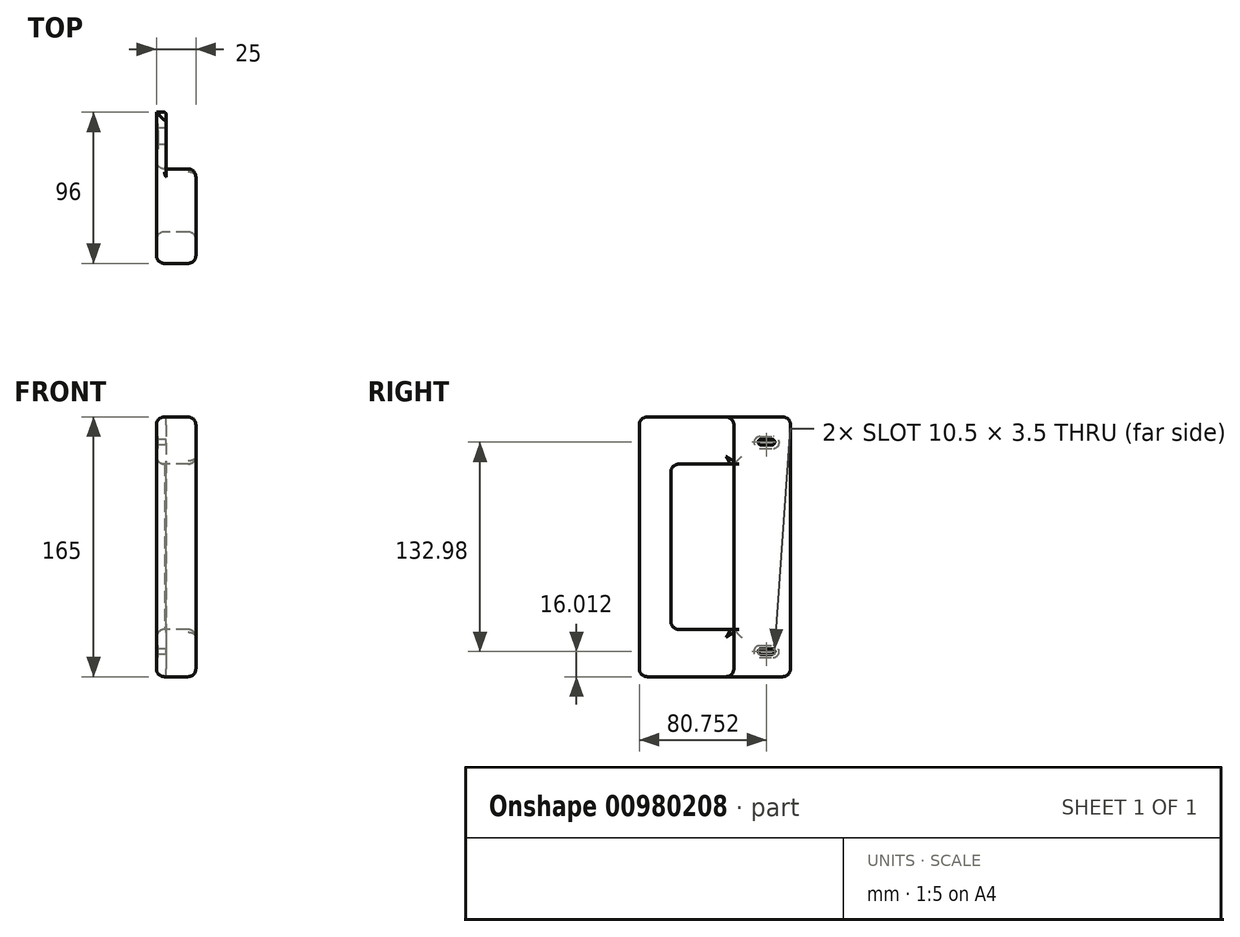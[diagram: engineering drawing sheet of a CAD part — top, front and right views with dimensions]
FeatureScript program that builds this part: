
annotation { "Feature Type Name" : "Feature", "Feature Type Description" : "" }
export const myFeature = defineFeature(function(context is Context, id is Id, definition is map)
    precondition{}
    {
        {
            var Q0;
            Q0=qCreatedBy(makeId("Right.planeOp"),FACE);
            var sketch = newSketch(context, id + "F0", { "sketchPlane" : qUnion([Q0])});
            skLineSegment(sketch, "E0.bottom", {"start": v(74.02, 103.51) * mm, "end": v(38.02, 103.51) * mm});
            skLineSegment(sketch, "E0.top", {"start": v(74.02, -61.49) * mm, "end": v(38.02, -61.49) * mm});
            skLineSegment(sketch, "E0.left", {"start": v(74.02, 103.51) * mm, "end": v(74.02, -61.49) * mm});
            skLineSegment(sketch, "E0.right", {"start": v(38.02, 103.51) * mm, "end": v(38.02, -61.49) * mm});
            skLineSegment(sketch, "E1", {"start": v(74.02, 21.01) * mm, "end": v(38.02, 21.01) * mm, "construction": true});
            skArc(sketch, "E2.0.startCap", {"start": v(62.27, 89.25) * mm, "mid": v(64.02, 87.5) * mm, "end": v(62.27, 85.75) * mm});
            skPoint(sketch, "E3", {"position": v(64.02, 87.5) * mm});
            skPoint(sketch, "E4", {"position": v(53.52, 87.5) * mm});
            skArc(sketch, "E5.0.startCap", {"start": v(55.27, 85.75) * mm, "mid": v(53.52, 87.5) * mm, "end": v(55.27, 89.25) * mm});
            skLineSegment(sketch, "E6", {"start": v(62.27, 89.25) * mm, "end": v(55.27, 89.25) * mm});
            skLineSegment(sketch, "E7", {"start": v(55.27, 85.75) * mm, "end": v(62.27, 85.75) * mm});
            skArc(sketch, "E8.MirrorCS", {"start": v(55.27, -43.73) * mm, "mid": v(53.52, -45.48) * mm, "end": v(55.27, -47.23) * mm});
            skArc(sketch, "E9.MirrorCS", {"start": v(62.27, -47.23) * mm, "mid": v(64.02, -45.48) * mm, "end": v(62.27, -43.73) * mm});
            skPoint(sketch, "E10.MirrorP", {"position": v(64.02, -45.48) * mm});
            skLineSegment(sketch, "E11.MirrorCS", {"start": v(62.27, -47.23) * mm, "end": v(55.27, -47.23) * mm});
            skLineSegment(sketch, "E12.MirrorCS", {"start": v(55.27, -43.73) * mm, "end": v(62.27, -43.73) * mm});
            skLineSegment(sketch, "E13.MirrorCS", {"start": v(74.02, -61.49) * mm, "end": v(74.02, 103.51) * mm});
            skSolve(sketch);
        }
        {
            var Q0;
            Q0=qCreatedBy(makeId("Right.planeOp"),FACE);
            var sketch = newSketch(context, id + "F1", { "sketchPlane" : qUnion([Q0])});
            skLineSegment(sketch, "E14.bottom", {"start": v(38.02, 103.51) * mm, "end": v(-21.98, 103.51) * mm});
            skLineSegment(sketch, "E14.top", {"start": v(38.02, -61.49) * mm, "end": v(-21.98, -61.49) * mm});
            skLineSegment(sketch, "E14.left", {"start": v(38.02, 103.51) * mm, "end": v(38.02, -61.49) * mm});
            skLineSegment(sketch, "E14.right", {"start": v(-21.98, 103.51) * mm, "end": v(-21.98, -61.49) * mm});
            skLineSegment(sketch, "E15.bottom", {"start": v(38.02, 73.51) * mm, "end": v(-1.98, 73.51) * mm});
            skLineSegment(sketch, "E15.top", {"start": v(38.02, -31.49) * mm, "end": v(-1.98, -31.49) * mm});
            skLineSegment(sketch, "E15.left", {"start": v(38.02, 73.51) * mm, "end": v(38.02, -31.49) * mm});
            skLineSegment(sketch, "E15.right", {"start": v(-1.98, 73.51) * mm, "end": v(-1.98, -31.49) * mm});
            skLineSegment(sketch, "E16", {"start": v(-21.98, 21.01) * mm, "end": v(38.02, 21.01) * mm, "construction": true});
            skSolve(sketch);
        }
        {
            var Q0;
            {var subQ4=sQuery(id+"F1.wireOp",EDGE,"E14.bottom");Q0=makeQuery(id+"F1.imprint","IMPRINT",FACE,{"disambiguationData":[TD([[makeQuery(id+"F1.imprint","IMPRINT",EDGE,{"derivedFrom":subQ4}),1.0]])]});}
            extrude(context, id + "F2", {"entities" : qUnion([Q0]), "depth" : 25 * mm, "offsetDistance" : 25 * mm});
        }
        {
            var Q0;
            Q0=makeQuery(id+"F0.imprint","IMPRINT",FACE,{"disambiguationData":[TD([[makeQuery(id+"F0.imprint","IMPRINT",EDGE,{"derivedFrom":sQuery(id+"F0.wireOp",EDGE,"E0.bottom")}),1.0]])]});
            extrude(context, id + "F3", {"entities" : qUnion([Q0]), "operationType" : NewBodyOperationType.ADD, "depth" : 6 * mm, "offsetDistance" : 25 * mm});
        }
        {
            var Q0;
            Q0=qCreatedBy(makeId("Right.planeOp"),FACE);
            var sketch = newSketch(context, id + "F4", { "sketchPlane" : qUnion([Q0])});
            skLineSegment(sketch, "E17", {"start": v(54.6, 91.01) * mm, "end": v(63.15, 91.01) * mm});
            skLineSegment(sketch, "E18", {"start": v(54.6, 83.51) * mm, "end": v(63.15, 83.51) * mm});
            skArc(sketch, "E19", {"start": v(63.15, 91.01) * mm, "mid": v(66.9, 87.26) * mm, "end": v(63.15, 83.51) * mm});
            skArc(sketch, "E20", {"start": v(54.6, 91.01) * mm, "mid": v(50.84, 87.26) * mm, "end": v(54.6, 83.51) * mm});
            skLineSegment(sketch, "E21", {"start": v(54.42, -41.78) * mm, "end": v(62.97, -41.78) * mm});
            skLineSegment(sketch, "E22", {"start": v(54.42, -49.28) * mm, "end": v(62.97, -49.28) * mm});
            skArc(sketch, "E23", {"start": v(62.97, -41.78) * mm, "mid": v(66.72, -45.53) * mm, "end": v(62.97, -49.28) * mm});
            skArc(sketch, "E24", {"start": v(54.42, -41.78) * mm, "mid": v(50.67, -45.53) * mm, "end": v(54.42, -49.28) * mm});
            skSolve(sketch);
        }
        {
            var Q0;
            Q0 = qSketchRegion(id + "F4", true);
            extrude(context, id + "F5", {"entities" : qUnion([Q0]), "operationType" : NewBodyOperationType.REMOVE, "oppositeDirection" : true, "depth" : -1 * mm, "offsetDistance" : 25 * mm});
        }
        {
            var Q0;
            Q0=makeQuery(id+"F2.opExtrude","CAP_EDGE",EDGE,{"disambiguationData":[OSD([sQuery(id+"F1.wireOp",EDGE,"E15.right")])],"isStart":true});
            var Q1;
            Q1=makeQuery(id+"F2.opExtrude","CAP_EDGE",EDGE,{"disambiguationData":[OSD([sQuery(id+"F1.wireOp",EDGE,"E15.top")])],"isStart":true});
            var Q2;
            Q2=makeQuery(id+"F3.opExtrude","CAP_EDGE",EDGE,{"disambiguationData":[OSD([sQuery(id+"F0.wireOp",EDGE,"E0.right")])],"isStart":true});
            var Q3;
            Q3=makeQuery(id+"F2.opExtrude","CAP_EDGE",EDGE,{"disambiguationData":[OSD([sQuery(id+"F1.wireOp",EDGE,"E15.bottom")])],"isStart":true});
            var Q4;
            Q4=makeQuery(id+"F2.opExtrude","CAP_EDGE",EDGE,{"disambiguationData":[OSD([sQuery(id+"F1.wireOp",EDGE,"E15.right")])],"isStart":false});
            var Q5;
            Q5=makeQuery(id+"F2.opExtrude","CAP_EDGE",EDGE,{"disambiguationData":[OSD([sQuery(id+"F1.wireOp",EDGE,"E15.top")])],"isStart":false});
            var Q6;
            {var subQ0=sQuery(id+"F1.wireOp",EDGE,"E14.left");Q6=makeQuery(id+"F2.opExtrude","CAP_EDGE",EDGE,{"disambiguationData":[OSD([subQ0]),TDD([makeQuery(id+"F1.imprint","IMPRINT",EDGE,{"disambiguationData":[TD([[makeQuery(id+"F1.imprint","INTERSECT",VERTEX,{"derivedFrom":[sQuery(id+"F1.wireOp",EDGE,"E14.top"),subQ0]}),1.0]])],"derivedFrom":subQ0})])],"isStart":false});}
            var Q7;
            Q7=makeQuery(id+"F2.opExtrude","CAP_EDGE",EDGE,{"disambiguationData":[OSD([sQuery(id+"F1.wireOp",EDGE,"E15.bottom")])],"isStart":false});
            var Q8;
            Q8=makeQuery(id+"F2.opExtrude","SWEPT_EDGE",EDGE,{"disambiguationData":[OSD([sQuery(id+"F1.wireOp",EDGE,"E14.bottom"),sQuery(id+"F1.wireOp",EDGE,"E14.left")])]});
            var Q9;
            {var subQ0=sQuery(id+"F1.wireOp",EDGE,"E14.left");Q9=makeQuery(id+"F2.opExtrude","CAP_EDGE",EDGE,{"disambiguationData":[OSD([subQ0]),TDD([makeQuery(id+"F1.imprint","IMPRINT",EDGE,{"disambiguationData":[TD([[makeQuery(id+"F1.imprint","INTERSECT",VERTEX,{"derivedFrom":[sQuery(id+"F1.wireOp",EDGE,"E14.bottom"),subQ0]}),-1.0]])],"derivedFrom":subQ0})])],"isStart":false});}
            var Q10;
            Q10=makeQuery(id+"F2.opExtrude","CAP_EDGE",EDGE,{"disambiguationData":[OSD([sQuery(id+"F1.wireOp",EDGE,"E14.bottom")])],"isStart":false});
            var Q11;
            Q11=makeQuery(id+"F2.boolean.opBoolean","MERGE",EDGE,{"derivedFrom":[makeQuery(id+"F3.opExtrude","CAP_EDGE",EDGE,{"disambiguationData":[OSD([sQuery(id+"F0.wireOp",EDGE,"E0.bottom")])],"isStart":true}),makeQuery(id+"F2.opExtrude","CAP_EDGE",EDGE,{"disambiguationData":[OSD([sQuery(id+"F1.wireOp",EDGE,"E14.bottom")])],"isStart":true})]});
            var Q12;
            Q12=makeQuery(id+"F2.opExtrude","SWEPT_EDGE",EDGE,{"disambiguationData":[OSD([sQuery(id+"F1.wireOp",EDGE,"E14.bottom"),sQuery(id+"F1.wireOp",EDGE,"E14.right")])]});
            var Q13;
            Q13=makeQuery(id+"F2.opExtrude","CAP_EDGE",EDGE,{"disambiguationData":[OSD([sQuery(id+"F1.wireOp",EDGE,"E14.right")])],"isStart":false});
            var Q14;
            Q14=makeQuery(id+"F2.opExtrude","CAP_EDGE",EDGE,{"disambiguationData":[OSD([sQuery(id+"F1.wireOp",EDGE,"E14.right")])],"isStart":true});
            var Q15;
            Q15=makeQuery(id+"F2.boolean.opBoolean","MERGE",EDGE,{"derivedFrom":[makeQuery(id+"F3.opExtrude","CAP_EDGE",EDGE,{"disambiguationData":[OSD([sQuery(id+"F0.wireOp",EDGE,"E0.top")])],"isStart":true}),makeQuery(id+"F2.opExtrude","CAP_EDGE",EDGE,{"disambiguationData":[OSD([sQuery(id+"F1.wireOp",EDGE,"E14.top")])],"isStart":true})]});
            var Q16;
            Q16=makeQuery(id+"F2.opExtrude","SWEPT_EDGE",EDGE,{"disambiguationData":[OSD([sQuery(id+"F1.wireOp",EDGE,"E14.top"),sQuery(id+"F1.wireOp",EDGE,"E14.right")])]});
            var Q17;
            Q17=makeQuery(id+"F2.opExtrude","CAP_EDGE",EDGE,{"disambiguationData":[OSD([sQuery(id+"F1.wireOp",EDGE,"E14.top")])],"isStart":false});
            var Q18;
            Q18=makeQuery(id+"F2.opExtrude","SWEPT_EDGE",EDGE,{"disambiguationData":[OSD([sQuery(id+"F1.wireOp",EDGE,"E14.top"),sQuery(id+"F1.wireOp",EDGE,"E14.left")])]});
            var Q19;
            Q19=makeQuery(id+"F2.opExtrude","SWEPT_EDGE",EDGE,{"disambiguationData":[OSD([sQuery(id+"F1.wireOp",EDGE,"E15.top"),sQuery(id+"F1.wireOp",EDGE,"E15.right")])]});
            var Q20;
            Q20=makeQuery(id+"F2.opExtrude","SWEPT_EDGE",EDGE,{"disambiguationData":[OSD([sQuery(id+"F1.wireOp",EDGE,"E15.bottom"),sQuery(id+"F1.wireOp",EDGE,"E15.right")])]});
            var Q21;
            Q21=makeQuery(id+"F3.opExtrude","SWEPT_EDGE",EDGE,{"disambiguationData":[OSD([sQuery(id+"F0.wireOp",EDGE,"E0.top"),sQuery(id+"F0.wireOp",EDGE,"E13.MirrorCS")])]});
            var Q22;
            Q22=makeQuery(id+"F3.opExtrude","SWEPT_EDGE",EDGE,{"disambiguationData":[OSD([sQuery(id+"F0.wireOp",EDGE,"E0.bottom"),sQuery(id+"F0.wireOp",EDGE,"E13.MirrorCS")])]});
            var Q23;
            Q23=makeQuery(id+"F3.opExtrude","CAP_EDGE",EDGE,{"disambiguationData":[OSD([sQuery(id+"F0.wireOp",EDGE,"E13.MirrorCS")])],"isStart":true});
            fillet(context, id + "F6", {"entities" : qUnion([Q0, Q1, Q2, Q3, Q4, Q5, Q6, Q7, Q8, Q9, Q10, Q11, Q12, Q13, Q14, Q15, Q16, Q17, Q18, Q19, Q20, Q21, Q22, Q23]), "radius" : 5 * mm, "tangentPropagation" : true, "allowEdgeOverflow" : false});
        }
        {
            var Q0;
            Q0=makeQuery(id+"F3.opExtrude","CAP_EDGE",EDGE,{"disambiguationData":[OSD([sQuery(id+"F0.wireOp",EDGE,"E0.bottom")])],"isStart":false});
            var Q1;
            Q1=makeQuery(id+"F3.opExtrude","CAP_EDGE",EDGE,{"disambiguationData":[OSD([sQuery(id+"F0.wireOp",EDGE,"E13.MirrorCS")])],"isStart":false});
            var Q2;
            Q2=makeQuery(id+"F6.opFillet","BLEND_EDGE",EDGE,{"blendedFrom":[makeQuery(id+"F2.boolean.opBoolean","MERGE",EDGE,{"derivedFrom":[makeQuery(id+"F3.opExtrude","CAP_EDGE",EDGE,{"disambiguationData":[OSD([sQuery(id+"F0.wireOp",EDGE,"E0.bottom")])],"isStart":true}),makeQuery(id+"F2.opExtrude","CAP_EDGE",EDGE,{"disambiguationData":[OSD([sQuery(id+"F1.wireOp",EDGE,"E14.bottom")])],"isStart":true})]}),makeQuery(id+"F3.opExtrude","SWEPT_FACE",FACE,{"disambiguationData":[OSD([sQuery(id+"F0.wireOp",EDGE,"E13.MirrorCS")])]})],"blendedInto":[makeQuery(id+"F3.opExtrude","SWEPT_FACE",FACE,{"disambiguationData":[OSD([sQuery(id+"F0.wireOp",EDGE,"E13.MirrorCS")])]})]});
            var Q3;
            Q3=makeQuery(id+"F3.opExtrude","CAP_EDGE",EDGE,{"disambiguationData":[OSD([sQuery(id+"F0.wireOp",EDGE,"E0.top")])],"isStart":false});
            var Q4;
            {var subQ0=sQuery(id+"F1.wireOp",EDGE,"E15.top");var subQ1=sQuery(id+"F1.wireOp",EDGE,"E14.left");var subQ2=sQuery(id+"F0.wireOp",EDGE,"E0.right");Q4=makeQuery(id+"F6.opFillet","TWEAK_EDGE",EDGE,{"derivedFrom":[makeQuery(id+"F2.boolean.opBoolean","TWEAK_VERTEX",VERTEX,{"derivedFrom":[makeQuery(id+"F3.opExtrude","CAP_FACE",FACE,{"disambiguationData":[OSD([sQuery(id+"F0.wireOp",EDGE,"E0.bottom"),sQuery(id+"F0.wireOp",EDGE,"E0.top"),subQ2,sQuery(id+"F0.wireOp",EDGE,"E2.0.startCap"),sQuery(id+"F0.wireOp",EDGE,"E5.0.startCap"),sQuery(id+"F0.wireOp",EDGE,"E6"),sQuery(id+"F0.wireOp",EDGE,"E7"),sQuery(id+"F0.wireOp",EDGE,"E8.MirrorCS"),sQuery(id+"F0.wireOp",EDGE,"E9.MirrorCS"),sQuery(id+"F0.wireOp",EDGE,"E11.MirrorCS"),sQuery(id+"F0.wireOp",EDGE,"E12.MirrorCS"),sQuery(id+"F0.wireOp",EDGE,"E13.MirrorCS")])],"isStart":false}),makeQuery(id+"F3.opExtrude","SWEPT_FACE",FACE,{"disambiguationData":[OSD([subQ2])]}),makeQuery(id+"F2.opExtrude","SWEPT_FACE",FACE,{"disambiguationData":[OSD([subQ1]),TDD([makeQuery(id+"F1.imprint","IMPRINT",EDGE,{"disambiguationData":[TD([[makeQuery(id+"F1.imprint","INTERSECT",VERTEX,{"derivedFrom":[sQuery(id+"F1.wireOp",EDGE,"E14.top"),subQ1]}),1.0]])],"derivedFrom":subQ1})])]}),makeQuery(id+"F2.opExtrude","SWEPT_FACE",FACE,{"disambiguationData":[OSD([subQ0])]})]})]});}
            var Q5;
            {var subQ0=sQuery(id+"F1.wireOp",EDGE,"E15.bottom");var subQ1=sQuery(id+"F1.wireOp",EDGE,"E14.left");var subQ2=sQuery(id+"F0.wireOp",EDGE,"E0.right");Q5=makeQuery(id+"F6.opFillet","TWEAK_EDGE",EDGE,{"derivedFrom":[makeQuery(id+"F2.boolean.opBoolean","TWEAK_VERTEX",VERTEX,{"derivedFrom":[makeQuery(id+"F3.opExtrude","CAP_FACE",FACE,{"disambiguationData":[OSD([sQuery(id+"F0.wireOp",EDGE,"E0.bottom"),sQuery(id+"F0.wireOp",EDGE,"E0.top"),subQ2,sQuery(id+"F0.wireOp",EDGE,"E2.0.startCap"),sQuery(id+"F0.wireOp",EDGE,"E5.0.startCap"),sQuery(id+"F0.wireOp",EDGE,"E6"),sQuery(id+"F0.wireOp",EDGE,"E7"),sQuery(id+"F0.wireOp",EDGE,"E8.MirrorCS"),sQuery(id+"F0.wireOp",EDGE,"E9.MirrorCS"),sQuery(id+"F0.wireOp",EDGE,"E11.MirrorCS"),sQuery(id+"F0.wireOp",EDGE,"E12.MirrorCS"),sQuery(id+"F0.wireOp",EDGE,"E13.MirrorCS")])],"isStart":false}),makeQuery(id+"F3.opExtrude","SWEPT_FACE",FACE,{"disambiguationData":[OSD([subQ2])]}),makeQuery(id+"F2.opExtrude","SWEPT_FACE",FACE,{"disambiguationData":[OSD([subQ1]),TDD([makeQuery(id+"F1.imprint","IMPRINT",EDGE,{"disambiguationData":[TD([[makeQuery(id+"F1.imprint","INTERSECT",VERTEX,{"derivedFrom":[sQuery(id+"F1.wireOp",EDGE,"E14.bottom"),subQ1]}),-1.0]])],"derivedFrom":subQ1})])]}),makeQuery(id+"F2.opExtrude","SWEPT_FACE",FACE,{"disambiguationData":[OSD([subQ0])]})]})]});}
            var Q6;
            {var subQ0=sQuery(id+"F1.wireOp",EDGE,"E14.left");var subQ1=sQuery(id+"F1.wireOp",EDGE,"E15.left");var subQ2=sQuery(id+"F1.wireOp",EDGE,"E15.bottom");Q6=makeQuery(id+"F6.opFillet","BLEND_EDGE",EDGE,{"blendedFrom":[makeQuery(id+"F2.boolean.opBoolean","SPLIT",EDGE,{"disambiguationData":[topologyDisambiguationEdgeConnected([makeQuery(id+"F2.opExtrude","SWEPT_FACE",FACE,{"disambiguationData":[OSD([subQ0]),TDD([makeQuery(id+"F1.imprint","IMPRINT",EDGE,{"disambiguationData":[TD([[makeQuery(id+"F1.imprint","INTERSECT",VERTEX,{"derivedFrom":[sQuery(id+"F1.wireOp",EDGE,"E14.bottom"),subQ0]}),-1.0]])],"derivedFrom":subQ0})])]})])],"derivedFrom":makeQuery(id+"F2.opExtrude","SWEPT_EDGE",EDGE,{"disambiguationData":[OSD([subQ0,subQ2,subQ1])]})}),makeQuery(id+"F3.opExtrude","CAP_FACE",FACE,{"disambiguationData":[OSD([sQuery(id+"F0.wireOp",EDGE,"E0.bottom"),sQuery(id+"F0.wireOp",EDGE,"E0.top"),sQuery(id+"F0.wireOp",EDGE,"E0.right"),sQuery(id+"F0.wireOp",EDGE,"E2.0.startCap"),sQuery(id+"F0.wireOp",EDGE,"E5.0.startCap"),sQuery(id+"F0.wireOp",EDGE,"E6"),sQuery(id+"F0.wireOp",EDGE,"E7"),sQuery(id+"F0.wireOp",EDGE,"E8.MirrorCS"),sQuery(id+"F0.wireOp",EDGE,"E9.MirrorCS"),sQuery(id+"F0.wireOp",EDGE,"E11.MirrorCS"),sQuery(id+"F0.wireOp",EDGE,"E12.MirrorCS"),sQuery(id+"F0.wireOp",EDGE,"E13.MirrorCS")])],"isStart":false})],"blendedInto":[makeQuery(id+"F3.opExtrude","CAP_FACE",FACE,{"disambiguationData":[OSD([sQuery(id+"F0.wireOp",EDGE,"E0.bottom"),sQuery(id+"F0.wireOp",EDGE,"E0.top"),sQuery(id+"F0.wireOp",EDGE,"E0.right"),sQuery(id+"F0.wireOp",EDGE,"E2.0.startCap"),sQuery(id+"F0.wireOp",EDGE,"E5.0.startCap"),sQuery(id+"F0.wireOp",EDGE,"E6"),sQuery(id+"F0.wireOp",EDGE,"E7"),sQuery(id+"F0.wireOp",EDGE,"E8.MirrorCS"),sQuery(id+"F0.wireOp",EDGE,"E9.MirrorCS"),sQuery(id+"F0.wireOp",EDGE,"E11.MirrorCS"),sQuery(id+"F0.wireOp",EDGE,"E12.MirrorCS"),sQuery(id+"F0.wireOp",EDGE,"E13.MirrorCS")])],"isStart":false})]});}
            fillet(context, id + "F7", {"entities" : qUnion([Q0, Q1, Q2, Q3, Q4, Q5, Q6]), "radius" : 1 * mm, "tangentPropagation" : true, "allowEdgeOverflow" : false});
        }
        {
            var Q0;
            {var subQ0=sQuery(id+"F1.wireOp",EDGE,"E14.left");var subQ1=sQuery(id+"F0.wireOp",EDGE,"E0.right");Q0=makeQuery(id+"F3.boolean.opBoolean","SPLIT",EDGE,{"disambiguationData":[topologyDisambiguationEdgeConnected([makeQuery(id+"F2.opExtrude","SWEPT_FACE",FACE,{"disambiguationData":[OSD([subQ0]),TDD([makeQuery(id+"F1.imprint","IMPRINT",EDGE,{"disambiguationData":[TD([[makeQuery(id+"F1.imprint","INTERSECT",VERTEX,{"derivedFrom":[sQuery(id+"F1.wireOp",EDGE,"E14.bottom"),subQ0]}),-1.0]])],"derivedFrom":subQ0})])]})])],"derivedFrom":makeQuery(id+"F3.opExtrude","CAP_EDGE",EDGE,{"disambiguationData":[OSD([subQ1])],"isStart":false})});}
            var Q1;
            {var subQ0=sQuery(id+"F1.wireOp",EDGE,"E14.left");var subQ1=sQuery(id+"F0.wireOp",EDGE,"E0.right");Q1=makeQuery(id+"F3.boolean.opBoolean","SPLIT",EDGE,{"disambiguationData":[topologyDisambiguationEdgeConnected([makeQuery(id+"F2.opExtrude","SWEPT_FACE",FACE,{"disambiguationData":[OSD([subQ0]),TDD([makeQuery(id+"F1.imprint","IMPRINT",EDGE,{"disambiguationData":[TD([[makeQuery(id+"F1.imprint","INTERSECT",VERTEX,{"derivedFrom":[sQuery(id+"F1.wireOp",EDGE,"E14.top"),subQ0]}),1.0]])],"derivedFrom":subQ0})])]})])],"derivedFrom":makeQuery(id+"F3.opExtrude","CAP_EDGE",EDGE,{"disambiguationData":[OSD([subQ1])],"isStart":false})});}
            fillet(context, id + "F8", {"entities" : qUnion([Q0, Q1]), "radius" : 6 * mm, "tangentPropagation" : true, "allowEdgeOverflow" : false});
        }
        {
            var Q0;
            {var subQ0=sQuery(id+"F1.wireOp",EDGE,"E15.bottom");Q0=makeQuery(id+"F3.boolean.opBoolean","SPLIT",EDGE,{"disambiguationData":[topologyDisambiguationEdgeConnected([makeQuery(id+"F3.opExtrude","SWEPT_FACE",FACE,{"disambiguationData":[OSD([sQuery(id+"F0.wireOp",EDGE,"E0.right")])]})])],"derivedFrom":makeQuery(id+"F2.opExtrude","SWEPT_EDGE",EDGE,{"disambiguationData":[OSD([sQuery(id+"F1.wireOp",EDGE,"E14.left"),subQ0,sQuery(id+"F1.wireOp",EDGE,"E15.left")])]})});}
            var Q1;
            {var subQ0=sQuery(id+"F0.wireOp",EDGE,"E0.right");var subQ1=sQuery(id+"F1.wireOp",EDGE,"E15.bottom");var subQ2=sQuery(id+"F1.wireOp",EDGE,"E14.left");Q1=makeQuery(id+"F8.opFillet","TWEAK_EDGE",EDGE,{"derivedFrom":[makeQuery(id+"F3.boolean.opBoolean","TWEAK_VERTEX",VERTEX,{"derivedFrom":[makeQuery(id+"F2.opExtrude","SWEPT_FACE",FACE,{"disambiguationData":[OSD([subQ2]),TDD([makeQuery(id+"F1.imprint","IMPRINT",EDGE,{"disambiguationData":[TD([[makeQuery(id+"F1.imprint","INTERSECT",VERTEX,{"derivedFrom":[sQuery(id+"F1.wireOp",EDGE,"E14.bottom"),subQ2]}),-1.0]])],"derivedFrom":subQ2})])]}),makeQuery(id+"F2.opExtrude","SWEPT_FACE",FACE,{"disambiguationData":[OSD([subQ1])]}),makeQuery(id+"F3.opExtrude","CAP_FACE",FACE,{"disambiguationData":[OSD([sQuery(id+"F0.wireOp",EDGE,"E0.bottom"),sQuery(id+"F0.wireOp",EDGE,"E0.top"),subQ0,sQuery(id+"F0.wireOp",EDGE,"E2.0.startCap"),sQuery(id+"F0.wireOp",EDGE,"E5.0.startCap"),sQuery(id+"F0.wireOp",EDGE,"E6"),sQuery(id+"F0.wireOp",EDGE,"E7"),sQuery(id+"F0.wireOp",EDGE,"E8.MirrorCS"),sQuery(id+"F0.wireOp",EDGE,"E9.MirrorCS"),sQuery(id+"F0.wireOp",EDGE,"E11.MirrorCS"),sQuery(id+"F0.wireOp",EDGE,"E12.MirrorCS"),sQuery(id+"F0.wireOp",EDGE,"E13.MirrorCS")])],"isStart":false}),makeQuery(id+"F3.opExtrude","SWEPT_FACE",FACE,{"disambiguationData":[OSD([subQ0])]})]})]});}
            var Q2;
            {var subQ0=sQuery(id+"F1.wireOp",EDGE,"E15.top");Q2=makeQuery(id+"F3.boolean.opBoolean","SPLIT",EDGE,{"disambiguationData":[topologyDisambiguationEdgeConnected([makeQuery(id+"F3.opExtrude","SWEPT_FACE",FACE,{"disambiguationData":[OSD([sQuery(id+"F0.wireOp",EDGE,"E0.right")])]})])],"derivedFrom":makeQuery(id+"F2.opExtrude","SWEPT_EDGE",EDGE,{"disambiguationData":[OSD([sQuery(id+"F1.wireOp",EDGE,"E14.left"),subQ0,sQuery(id+"F1.wireOp",EDGE,"E15.left")])]})});}
            var Q3;
            {var subQ0=sQuery(id+"F0.wireOp",EDGE,"E0.right");var subQ1=sQuery(id+"F1.wireOp",EDGE,"E15.top");var subQ2=sQuery(id+"F1.wireOp",EDGE,"E14.left");Q3=makeQuery(id+"F8.opFillet","TWEAK_EDGE",EDGE,{"derivedFrom":[makeQuery(id+"F3.boolean.opBoolean","TWEAK_VERTEX",VERTEX,{"derivedFrom":[makeQuery(id+"F2.opExtrude","SWEPT_FACE",FACE,{"disambiguationData":[OSD([subQ2]),TDD([makeQuery(id+"F1.imprint","IMPRINT",EDGE,{"disambiguationData":[TD([[makeQuery(id+"F1.imprint","INTERSECT",VERTEX,{"derivedFrom":[sQuery(id+"F1.wireOp",EDGE,"E14.top"),subQ2]}),1.0]])],"derivedFrom":subQ2})])]}),makeQuery(id+"F2.opExtrude","SWEPT_FACE",FACE,{"disambiguationData":[OSD([subQ1])]}),makeQuery(id+"F3.opExtrude","CAP_FACE",FACE,{"disambiguationData":[OSD([sQuery(id+"F0.wireOp",EDGE,"E0.bottom"),sQuery(id+"F0.wireOp",EDGE,"E0.top"),subQ0,sQuery(id+"F0.wireOp",EDGE,"E2.0.startCap"),sQuery(id+"F0.wireOp",EDGE,"E5.0.startCap"),sQuery(id+"F0.wireOp",EDGE,"E6"),sQuery(id+"F0.wireOp",EDGE,"E7"),sQuery(id+"F0.wireOp",EDGE,"E8.MirrorCS"),sQuery(id+"F0.wireOp",EDGE,"E9.MirrorCS"),sQuery(id+"F0.wireOp",EDGE,"E11.MirrorCS"),sQuery(id+"F0.wireOp",EDGE,"E12.MirrorCS"),sQuery(id+"F0.wireOp",EDGE,"E13.MirrorCS")])],"isStart":false}),makeQuery(id+"F3.opExtrude","SWEPT_FACE",FACE,{"disambiguationData":[OSD([subQ0])]})]})]});}
            fillet(context, id + "F9", {"entities" : qUnion([Q0, Q1, Q2, Q3]), "radius" : 2 * mm, "tangentPropagation" : true, "allowEdgeOverflow" : false});
        }
    });
